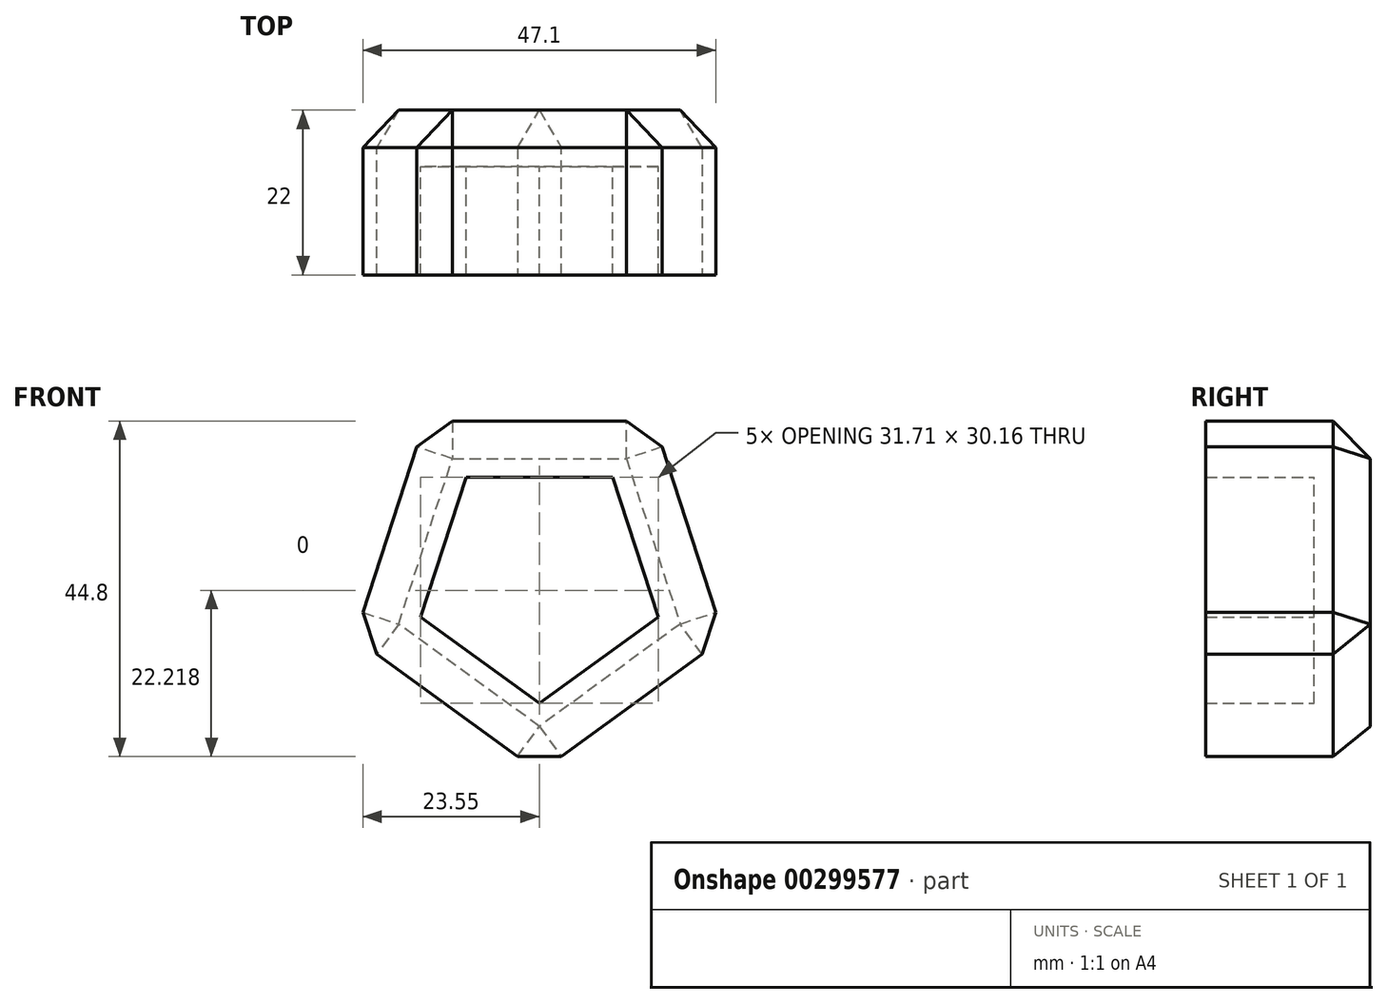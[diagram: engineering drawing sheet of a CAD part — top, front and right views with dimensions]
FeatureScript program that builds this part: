
annotation { "Feature Type Name" : "Feature", "Feature Type Description" : "" }
export const myFeature = defineFeature(function(context is Context, id is Id, definition is map)
    precondition{}
    {
        {
            var Q0;
            Q0=qCreatedBy(makeId("Front.planeOp"),FACE);
            var sketch = newSketch(context, id + "F0", { "sketchPlane" : qUnion([Q0])});
            skCircle(sketch, "E0.cCircle", {"center": v(0, 0) * mm, "radius": 20.99 * mm, "construction": true});
            skLineSegment(sketch, "E0.0", {"start": v(-15.25, 20.99) * mm, "end": v(15.25, 20.99) * mm});
            skLineSegment(sketch, "E0.1", {"start": v(15.25, 20.99) * mm, "end": v(24.67, -8.02) * mm});
            skLineSegment(sketch, "E0.2", {"start": v(24.67, -8.02) * mm, "end": v(0, -25.94) * mm});
            skLineSegment(sketch, "E0.3", {"start": v(0, -25.94) * mm, "end": v(-24.67, -8.02) * mm});
            skLineSegment(sketch, "E0.4", {"start": v(-24.67, -8.02) * mm, "end": v(-15.25, 20.99) * mm});
            skPoint(sketch, "E0.0.midPoint", {"position": v(0, 20.99) * mm});
            skSolve(sketch);
        }
        {
            var Q0;
            Q0=makeQuery(id+"F0.imprint","IMPRINT",FACE,{"disambiguationData":[TD([[makeQuery(id+"F0.imprint","IMPRINT",EDGE,{"derivedFrom":sQuery(id+"F0.wireOp",EDGE,"E0.0")}),-1.0]])]});
            extrude(context, id + "F1", {"entities" : qUnion([Q0]), "depth" : 22 * mm});
        }
        {
            var Q0;
            Q0=makeQuery(id+"F1.opExtrude","CAP_FACE",FACE,{"disambiguationData":[OSD([sQuery(id+"F0.wireOp",EDGE,"E0.0"),sQuery(id+"F0.wireOp",EDGE,"E0.1"),sQuery(id+"F0.wireOp",EDGE,"E0.2"),sQuery(id+"F0.wireOp",EDGE,"E0.3"),sQuery(id+"F0.wireOp",EDGE,"E0.4")])],"isStart":false});
            shell(context, id + "F2", {"entities" : qUnion([Q0]), "thickness" : 7.5 * mm});
        }
        {
            var Q0;
            Q0=makeQuery(id+"F1.opExtrude","CAP_EDGE",EDGE,{"disambiguationData":[OSD([sQuery(id+"F0.wireOp",EDGE,"E0.4")])],"isStart":true});
            var Q1;
            Q1=makeQuery(id+"F1.opExtrude","CAP_EDGE",EDGE,{"disambiguationData":[OSD([sQuery(id+"F0.wireOp",EDGE,"E0.0")])],"isStart":true});
            var Q2;
            Q2=makeQuery(id+"F1.opExtrude","CAP_EDGE",EDGE,{"disambiguationData":[OSD([sQuery(id+"F0.wireOp",EDGE,"E0.1")])],"isStart":true});
            var Q3;
            Q3=makeQuery(id+"F1.opExtrude","CAP_EDGE",EDGE,{"disambiguationData":[OSD([sQuery(id+"F0.wireOp",EDGE,"E0.2")])],"isStart":true});
            var Q4;
            Q4=makeQuery(id+"F1.opExtrude","CAP_EDGE",EDGE,{"disambiguationData":[OSD([sQuery(id+"F0.wireOp",EDGE,"E0.3")])],"isStart":true});
            var Q5;
            Q5=makeQuery(id+"F1.opExtrude","SWEPT_EDGE",EDGE,{"disambiguationData":[OSD([sQuery(id+"F0.wireOp",EDGE,"E0.2"),sQuery(id+"F0.wireOp",EDGE,"E0.3")])]});
            var Q6;
            Q6=makeQuery(id+"F1.opExtrude","SWEPT_EDGE",EDGE,{"disambiguationData":[OSD([sQuery(id+"F0.wireOp",EDGE,"E0.1"),sQuery(id+"F0.wireOp",EDGE,"E0.2")])]});
            var Q7;
            Q7=makeQuery(id+"F1.opExtrude","SWEPT_EDGE",EDGE,{"disambiguationData":[OSD([sQuery(id+"F0.wireOp",EDGE,"E0.0"),sQuery(id+"F0.wireOp",EDGE,"E0.1")])]});
            var Q8;
            Q8=makeQuery(id+"F1.opExtrude","SWEPT_EDGE",EDGE,{"disambiguationData":[OSD([sQuery(id+"F0.wireOp",EDGE,"E0.0"),sQuery(id+"F0.wireOp",EDGE,"E0.4")])]});
            var Q9;
            Q9=makeQuery(id+"F1.opExtrude","SWEPT_EDGE",EDGE,{"disambiguationData":[OSD([sQuery(id+"F0.wireOp",EDGE,"E0.3"),sQuery(id+"F0.wireOp",EDGE,"E0.4")])]});
            chamfer(context, id + "F3", {"entities" : qUnion([Q0, Q1, Q2, Q3, Q4, Q5, Q6, Q7, Q8, Q9]), "width" : 5 * mm, "tangentPropagation" : true});
        }
    });
